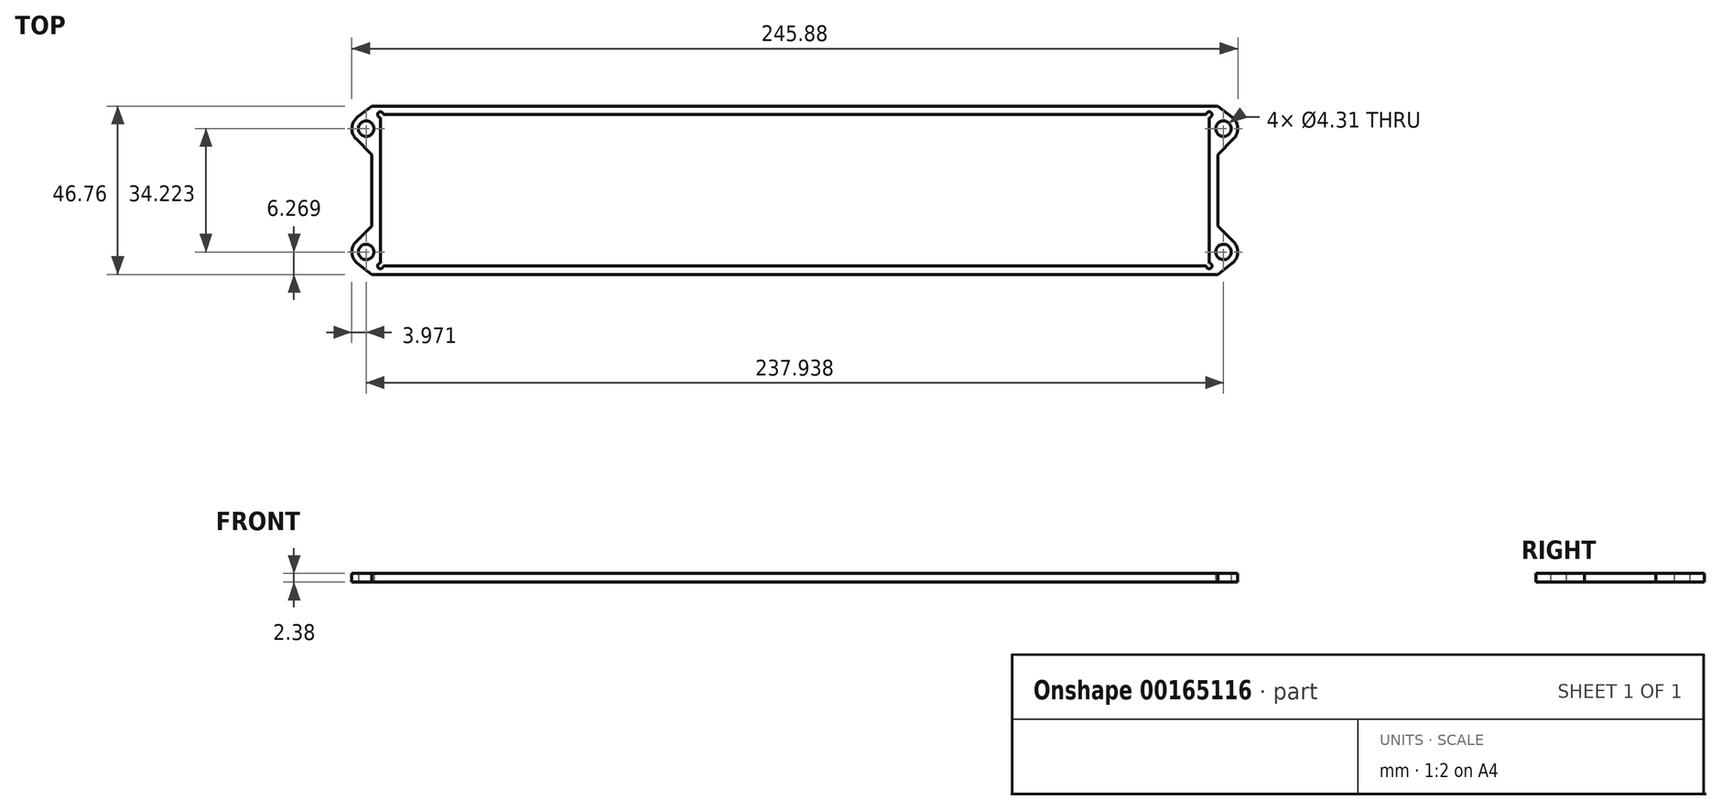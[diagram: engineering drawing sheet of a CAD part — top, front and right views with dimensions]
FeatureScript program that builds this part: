
annotation { "Feature Type Name" : "Feature", "Feature Type Description" : "" }
export const myFeature = defineFeature(function(context is Context, id is Id, definition is map)
    precondition{}
    {
        {
            var Q0;
            Q0=qCreatedBy(makeId("Top.planeOp"),FACE);
            var sketch = newSketch(context, id + "F0", { "sketchPlane" : qUnion([Q0])});
            skLineSegment(sketch, "E0.bottom", {"start": v(-115, 21) * mm, "end": v(115, 21) * mm});
            skLineSegment(sketch, "E0.top", {"start": v(-115, -21) * mm, "end": v(115, -21) * mm});
            skLineSegment(sketch, "E0.left", {"start": v(-115, 21) * mm, "end": v(-115, -21) * mm});
            skLineSegment(sketch, "E0.right", {"start": v(115, 21) * mm, "end": v(115, -21) * mm});
            skPoint(sketch, "E0.middle", {"position": v(0, 0) * mm});
            skLineSegment(sketch, "E1.bottom", {"start": v(-117.38, 23.38) * mm, "end": v(117.38, 23.38) * mm});
            skLineSegment(sketch, "E1.top", {"start": v(-117.38, -23.38) * mm, "end": v(117.38, -23.38) * mm});
            skLineSegment(sketch, "E1.left", {"start": v(-117.38, 23.38) * mm, "end": v(-117.38, -23.38) * mm});
            skLineSegment(sketch, "E1.right", {"start": v(117.38, 23.38) * mm, "end": v(117.38, -23.38) * mm});
            skLineSegment(sketch, "E2", {"start": v(-115, 21) * mm, "end": v(-117.38, 21) * mm, "construction": true});
            skLineSegment(sketch, "E3", {"start": v(-115, 21) * mm, "end": v(-115, 23.38) * mm, "construction": true});
            skSolve(sketch);
        }
        {
            var Q0;
            Q0=qSketchRegion(id+"F0",true);
            extrude(context, id + "F1", {"entities" : qUnion([Q0]), "depth" : 1 / 203.2 * mm});
        }
        {
            var Q0;
            Q0=makeQuery(id+"F1.opExtrude","CAP_FACE",FACE,{"disambiguationData":[OSD([sQuery(id+"F0.wireOp",EDGE,"E0.bottom"),sQuery(id+"F0.wireOp",EDGE,"E0.top"),sQuery(id+"F0.wireOp",EDGE,"E0.left"),sQuery(id+"F0.wireOp",EDGE,"E0.right"),sQuery(id+"F0.wireOp",EDGE,"E1.bottom"),sQuery(id+"F0.wireOp",EDGE,"E1.top"),sQuery(id+"F0.wireOp",EDGE,"E1.left"),sQuery(id+"F0.wireOp",EDGE,"E1.right")])],"isStart":true});
            var sketch = newSketch(context, id + "F2", { "sketchPlane" : qUnion([Q0])});
            skLineSegment(sketch, "E4.bottom", {"start": v(-117.38, 23.38) * mm, "end": v(117.38, 23.38) * mm});
            skLineSegment(sketch, "E4.top", {"start": v(-117.38, -23.38) * mm, "end": v(117.38, -23.38) * mm});
            skLineSegment(sketch, "E4.left", {"start": v(-117.38, 23.38) * mm, "end": v(-117.38, -23.38) * mm});
            skLineSegment(sketch, "E4.right", {"start": v(117.38, 23.38) * mm, "end": v(117.38, -23.38) * mm});
            skSolve(sketch);
        }
        {
            var Q0;
            Q0=qSketchRegion(id+"F2",true);
            extrude(context, id + "F3", {"entities" : qUnion([Q0]), "operationType" : NewBodyOperationType.ADD, "depth" : 2.38 * mm});
        }
        {
            var Q0;
            Q0=makeQuery(id+"F3.opExtrude","CAP_FACE",FACE,{"disambiguationData":[OSD([sQuery(id+"F2.wireOp",EDGE,"E4.bottom"),sQuery(id+"F2.wireOp",EDGE,"E4.top"),sQuery(id+"F2.wireOp",EDGE,"E4.left"),sQuery(id+"F2.wireOp",EDGE,"E4.right")])],"isStart":false});
            var sketch = newSketch(context, id + "F4", { "sketchPlane" : qUnion([Q0])});
            skLineSegment(sketch, "E5", {"start": v(-117.38, -23.38) * mm, "end": v(-121.4, -20.24) * mm});
            skLineSegment(sketch, "E6", {"start": v(-117.38, 23.38) * mm, "end": v(-121.4, 20.24) * mm});
            skArc(sketch, "E7", {"start": v(-121.78, -14.3) * mm, "mid": v(-122.93, -17.36) * mm, "end": v(-121.4, -20.24) * mm});
            skArc(sketch, "E8", {"start": v(-121.4, -20.24) * mm, "mid": v(-115, -16.87) * mm, "end": v(-121.78, -14.3) * mm, "construction": true});
            skLineSegment(sketch, "E9", {"start": v(-121.78, -14.3) * mm, "end": v(-117.38, -9.91) * mm});
            skArc(sketch, "E10", {"start": v(-121.4, 20.24) * mm, "mid": v(-122.93, 17.36) * mm, "end": v(-121.78, 14.3) * mm});
            skLineSegment(sketch, "E11", {"start": v(-121.78, 14.3) * mm, "end": v(-117.38, 9.91) * mm});
            skLineSegment(sketch, "E12", {"start": v(-117.38, -9.91) * mm, "end": v(-117.38, 9.91) * mm, "construction": true});
            skLineSegment(sketch, "E13", {"start": v(-117.38, 0) * mm, "end": v(117.38, 0) * mm, "construction": true});
            skLineSegment(sketch, "E14", {"start": v(117.38, -9.91) * mm, "end": v(117.38, 9.91) * mm, "construction": true});
            skLineSegment(sketch, "E15", {"start": v(-117.38, -23.38) * mm, "end": v(-117.38, -9.91) * mm});
            skLineSegment(sketch, "E16", {"start": v(-117.38, 9.91) * mm, "end": v(-117.38, 23.38) * mm});
            skLineSegment(sketch, "E17", {"start": v(117.38, -23.38) * mm, "end": v(121.4, -20.24) * mm});
            skLineSegment(sketch, "E18", {"start": v(117.38, 23.38) * mm, "end": v(121.4, 20.24) * mm});
            skLineSegment(sketch, "E19", {"start": v(117.38, 9.91) * mm, "end": v(121.78, 14.3) * mm});
            skLineSegment(sketch, "E20", {"start": v(117.38, -9.91) * mm, "end": v(121.78, -14.3) * mm});
            skArc(sketch, "E21", {"start": v(121.4, -20.24) * mm, "mid": v(122.93, -17.36) * mm, "end": v(121.78, -14.3) * mm});
            skArc(sketch, "E22", {"start": v(121.78, 14.3) * mm, "mid": v(122.93, 17.36) * mm, "end": v(121.4, 20.24) * mm});
            skLineSegment(sketch, "E23", {"start": v(117.38, -23.38) * mm, "end": v(117.38, -9.91) * mm});
            skLineSegment(sketch, "E24", {"start": v(117.38, 9.91) * mm, "end": v(117.38, 23.38) * mm});
            skCircle(sketch, "E25", {"center": v(-115, -21) * mm, "radius": 1.59 * mm, "construction": true});
            skSolve(sketch);
        }
        {
            var Q0;
            Q0 = qSketchRegion(id + "F4", true);
            var Q1;
            Q1=makeQuery(id+"F1.opExtrude","CAP_FACE",FACE,{"disambiguationData":[OSD([sQuery(id+"F0.wireOp",EDGE,"E0.bottom"),sQuery(id+"F0.wireOp",EDGE,"E0.top"),sQuery(id+"F0.wireOp",EDGE,"E0.left"),sQuery(id+"F0.wireOp",EDGE,"E0.right"),sQuery(id+"F0.wireOp",EDGE,"E1.bottom"),sQuery(id+"F0.wireOp",EDGE,"E1.top"),sQuery(id+"F0.wireOp",EDGE,"E1.left"),sQuery(id+"F0.wireOp",EDGE,"E1.right")])],"isStart":false});
            extrude(context, id + "F5", {"entities" : qUnion([Q0]), "operationType" : NewBodyOperationType.ADD, "endBound" : BoundingType.UP_TO_SURFACE, "oppositeDirection" : true, "endBoundEntityFace" : qUnion([Q1]), "depth" : 25.4 * mm});
        }
        {
            var Q0;
            Q0=makeQuery(id+"F5.boolean.opBoolean","MERGE",FACE,{"derivedFrom":[makeQuery(id+"F3.opExtrude","CAP_FACE",FACE,{"disambiguationData":[OSD([sQuery(id+"F2.wireOp",EDGE,"E4.bottom"),sQuery(id+"F2.wireOp",EDGE,"E4.top"),sQuery(id+"F2.wireOp",EDGE,"E4.left"),sQuery(id+"F2.wireOp",EDGE,"E4.right")])],"isStart":false}),makeQuery(id+"F5.opExtrude","CAP_FACE",FACE,{"disambiguationData":[OSD([sQuery(id+"F4.wireOp",EDGE,"E5"),sQuery(id+"F4.wireOp",EDGE,"E7"),sQuery(id+"F4.wireOp",EDGE,"E9"),sQuery(id+"F4.wireOp",EDGE,"E15")])],"isStart":true}),makeQuery(id+"F5.opExtrude","CAP_FACE",FACE,{"disambiguationData":[OSD([sQuery(id+"F4.wireOp",EDGE,"E6"),sQuery(id+"F4.wireOp",EDGE,"E10"),sQuery(id+"F4.wireOp",EDGE,"E11"),sQuery(id+"F4.wireOp",EDGE,"E16")])],"isStart":true}),makeQuery(id+"F5.opExtrude","CAP_FACE",FACE,{"disambiguationData":[OSD([sQuery(id+"F4.wireOp",EDGE,"E17"),sQuery(id+"F4.wireOp",EDGE,"E20"),sQuery(id+"F4.wireOp",EDGE,"E21"),sQuery(id+"F4.wireOp",EDGE,"E23")])],"isStart":true}),makeQuery(id+"F5.opExtrude","CAP_FACE",FACE,{"disambiguationData":[OSD([sQuery(id+"F4.wireOp",EDGE,"E18"),sQuery(id+"F4.wireOp",EDGE,"E19"),sQuery(id+"F4.wireOp",EDGE,"E22"),sQuery(id+"F4.wireOp",EDGE,"E24")])],"isStart":true})]});
            var sketch = newSketch(context, id + "F6", { "sketchPlane" : qUnion([Q0])});
            skCircle(sketch, "E26", {"center": v(-118.97, -17.11) * mm, "radius": 2.15 * mm});
            skCircle(sketch, "E27", {"center": v(-118.97, 17.11) * mm, "radius": 2.15 * mm});
            skCircle(sketch, "E28", {"center": v(118.97, 17.11) * mm, "radius": 2.15 * mm});
            skCircle(sketch, "E29", {"center": v(118.97, -17.11) * mm, "radius": 2.15 * mm});
            skSolve(sketch);
        }
        {
            var Q0;
            Q0 = qSketchRegion(id + "F6", true);
            var Q1;
            Q1=makeQuery(id+"F5.boolean.opBoolean","MERGE",FACE,{"derivedFrom":[makeQuery(id+"F1.opExtrude","CAP_FACE",FACE,{"disambiguationData":[OSD([sQuery(id+"F0.wireOp",EDGE,"E0.bottom"),sQuery(id+"F0.wireOp",EDGE,"E0.top"),sQuery(id+"F0.wireOp",EDGE,"E0.left"),sQuery(id+"F0.wireOp",EDGE,"E0.right"),sQuery(id+"F0.wireOp",EDGE,"E1.bottom"),sQuery(id+"F0.wireOp",EDGE,"E1.top"),sQuery(id+"F0.wireOp",EDGE,"E1.left"),sQuery(id+"F0.wireOp",EDGE,"E1.right")])],"isStart":false}),makeQuery(id+"F5.opExtrude","CAP_FACE",FACE,{"disambiguationData":[OSD([sQuery(id+"F4.wireOp",EDGE,"E5"),sQuery(id+"F4.wireOp",EDGE,"E7"),sQuery(id+"F4.wireOp",EDGE,"E9"),sQuery(id+"F4.wireOp",EDGE,"E15")])],"isStart":false}),makeQuery(id+"F5.opExtrude","CAP_FACE",FACE,{"disambiguationData":[OSD([sQuery(id+"F4.wireOp",EDGE,"E6"),sQuery(id+"F4.wireOp",EDGE,"E10"),sQuery(id+"F4.wireOp",EDGE,"E11"),sQuery(id+"F4.wireOp",EDGE,"E16")])],"isStart":false}),makeQuery(id+"F5.opExtrude","CAP_FACE",FACE,{"disambiguationData":[OSD([sQuery(id+"F4.wireOp",EDGE,"E17"),sQuery(id+"F4.wireOp",EDGE,"E20"),sQuery(id+"F4.wireOp",EDGE,"E21"),sQuery(id+"F4.wireOp",EDGE,"E23")])],"isStart":false}),makeQuery(id+"F5.opExtrude","CAP_FACE",FACE,{"disambiguationData":[OSD([sQuery(id+"F4.wireOp",EDGE,"E18"),sQuery(id+"F4.wireOp",EDGE,"E19"),sQuery(id+"F4.wireOp",EDGE,"E22"),sQuery(id+"F4.wireOp",EDGE,"E24")])],"isStart":false})]});
            extrude(context, id + "F7", {"entities" : qUnion([Q0]), "operationType" : NewBodyOperationType.REMOVE, "endBound" : BoundingType.UP_TO_SURFACE, "oppositeDirection" : true, "endBoundEntityFace" : qUnion([Q1]), "depth" : 25.4 * mm});
        }
        {
            var Q0;
            Q0=makeQuery(id+"F5.boolean.opBoolean","MERGE",FACE,{"derivedFrom":[makeQuery(id+"F1.opExtrude","CAP_FACE",FACE,{"disambiguationData":[OSD([sQuery(id+"F0.wireOp",EDGE,"E0.bottom"),sQuery(id+"F0.wireOp",EDGE,"E0.top"),sQuery(id+"F0.wireOp",EDGE,"E0.left"),sQuery(id+"F0.wireOp",EDGE,"E0.right"),sQuery(id+"F0.wireOp",EDGE,"E1.bottom"),sQuery(id+"F0.wireOp",EDGE,"E1.top"),sQuery(id+"F0.wireOp",EDGE,"E1.left"),sQuery(id+"F0.wireOp",EDGE,"E1.right")])],"isStart":false}),makeQuery(id+"F5.opExtrude","CAP_FACE",FACE,{"disambiguationData":[OSD([sQuery(id+"F4.wireOp",EDGE,"E5"),sQuery(id+"F4.wireOp",EDGE,"E7"),sQuery(id+"F4.wireOp",EDGE,"E9"),sQuery(id+"F4.wireOp",EDGE,"E15")])],"isStart":false}),makeQuery(id+"F5.opExtrude","CAP_FACE",FACE,{"disambiguationData":[OSD([sQuery(id+"F4.wireOp",EDGE,"E6"),sQuery(id+"F4.wireOp",EDGE,"E10"),sQuery(id+"F4.wireOp",EDGE,"E11"),sQuery(id+"F4.wireOp",EDGE,"E16")])],"isStart":false}),makeQuery(id+"F5.opExtrude","CAP_FACE",FACE,{"disambiguationData":[OSD([sQuery(id+"F4.wireOp",EDGE,"E17"),sQuery(id+"F4.wireOp",EDGE,"E20"),sQuery(id+"F4.wireOp",EDGE,"E21"),sQuery(id+"F4.wireOp",EDGE,"E23")])],"isStart":false}),makeQuery(id+"F5.opExtrude","CAP_FACE",FACE,{"disambiguationData":[OSD([sQuery(id+"F4.wireOp",EDGE,"E18"),sQuery(id+"F4.wireOp",EDGE,"E19"),sQuery(id+"F4.wireOp",EDGE,"E22"),sQuery(id+"F4.wireOp",EDGE,"E24")])],"isStart":false})]});
            var sketch = newSketch(context, id + "F8", { "sketchPlane" : qUnion([Q0])});
            skCircle(sketch, "E30", {"center": v(-115, 21) * mm, "radius": 0.8 * mm});
            skCircle(sketch, "E31", {"center": v(-115, -21) * mm, "radius": 0.8 * mm});
            skCircle(sketch, "E32", {"center": v(115, -21) * mm, "radius": 0.8 * mm});
            skCircle(sketch, "E33", {"center": v(115, 21) * mm, "radius": 0.8 * mm});
            skSolve(sketch);
        }
        {
            var Q0;
            Q0 = qSketchRegion(id + "F8", true);
            var Q1;
            Q1=makeQuery(id+"F3.opExtrude","CAP_FACE",FACE,{"disambiguationData":[OSD([sQuery(id+"F2.wireOp",EDGE,"E4.bottom"),sQuery(id+"F2.wireOp",EDGE,"E4.top"),sQuery(id+"F2.wireOp",EDGE,"E4.left"),sQuery(id+"F2.wireOp",EDGE,"E4.right")])],"isStart":true});
            extrude(context, id + "F9", {"entities" : qUnion([Q0]), "operationType" : NewBodyOperationType.REMOVE, "endBound" : BoundingType.UP_TO_SURFACE, "oppositeDirection" : true, "endBoundEntityFace" : qUnion([Q1]), "depth" : 25.4 * mm});
        }
    });
